FCSTD DOCUMENT  (FreeCAD 0.19R22756 (Git))
Label: housing
License: All rights reserved
LicenseURL: http://en.wikipedia.org/wiki/All_rights_reserved
objects: Part::Part2DObjectPython×38, Part::Extrusion×25, Part::Box×21, Part::Cut×11, Part::Cylinder×8, App::Part×8, Part::Compound×1, App::LinkGroup×1, Part::FeaturePython×1
note: 104 computed .brp shape members not serialized (recipe doc carries the construction recipe); baked Part::Feature solids carry a one-line shape summary decoded from their .brp

FEATURE [Part::Box] Box003  label="Cube003"
  AttacherType = Attacher::AttachEngine3D
  Height = 14
  Length = 125
  Placement = pos=(2,0,1) rot=(0,0,1;1.5708rad)
  Width = 1
FEATURE [Part::Box] Box006  label="Cube006"
  AttacherType = Attacher::AttachEngine3D
  Height = 1
  Length = 118
  Placement = pos=(1,1,1) rot=(0,0,1;0rad)
  Width = 123
FEATURE [Part::Cylinder] Cylinder
  Angle = 360
  AttacherType = Attacher::AttachEngine3D
  Height = 1.6
  Placement = pos=(0,0,5) rot=(0,0,1;0rad)
  Radius = 1
FEATURE [Part::Cylinder] Cylinder001
  Angle = 360
  AttacherType = Attacher::AttachEngine3D
  Height = 3
  Placement = pos=(0,0,2) rot=(0,0,1;0rad)
  Radius = 2
FEATURE [App::Part] Part001  label="Pod"
  Group = -> [Cylinder001,Cylinder]
  Origin = -> Origin001
  Placement = pos=(4.5,92,-1) rot=(0,0,1;0rad)
FEATURE [Part::Cylinder] Cylinder002
  Angle = 360
  AttacherType = Attacher::AttachEngine3D
  Height = 3
  Placement = pos=(0,0,2) rot=(0,0,1;0rad)
  Radius = 2
FEATURE [Part::Cylinder] Cylinder003
  Angle = 360
  AttacherType = Attacher::AttachEngine3D
  Height = 1.6
  Placement = pos=(0,0,5) rot=(0,0,1;0rad)
  Radius = 1
FEATURE [App::Part] Part002  label="Pod001"
  Group = -> [Cylinder002,Cylinder003]
  Origin = -> Origin002
  Placement = pos=(4.5,67,-1) rot=(0,0,1;0rad)
FEATURE [Part::Cylinder] Cylinder004
  Angle = 360
  AttacherType = Attacher::AttachEngine3D
  Height = 3
  Placement = pos=(0,0,2) rot=(0,0,1;0rad)
  Radius = 2
FEATURE [Part::Cylinder] Cylinder005
  Angle = 360
  AttacherType = Attacher::AttachEngine3D
  Height = 3
  Placement = pos=(0,0,2) rot=(0,0,1;0rad)
  Radius = 2
FEATURE [Part::Cylinder] Cylinder006
  Angle = 360
  AttacherType = Attacher::AttachEngine3D
  Height = 1.6
  Placement = pos=(0,0,5) rot=(0,0,1;0rad)
  Radius = 1
FEATURE [Part::Cylinder] Cylinder007
  Angle = 360
  AttacherType = Attacher::AttachEngine3D
  Height = 1.6
  Placement = pos=(0,0,5) rot=(0,0,1;0rad)
  Radius = 1
FEATURE [App::Part] Part003  label="Pod002"
  Group = -> [Cylinder004,Cylinder007]
  Origin = -> Origin003
  Placement = pos=(56.5,67,-1) rot=(0,0,1;0rad)
FEATURE [App::Part] Part004  label="Pod003"
  Group = -> [Cylinder005,Cylinder006]
  Origin = -> Origin004
  Placement = pos=(56.5,92,-1) rot=(0,0,1;0rad)
FEATURE [Part::Box] Box007  label="Cube007"
  AttacherType = Attacher::AttachEngine3D
  Height = 7
  Length = 2
  Placement = pos=(0,39,3.2) rot=(0,0,1;0rad)
  Width = 11
FEATURE [Part::Cut] Cut002
  Base = -> Box003
  Placement = pos=(118,0,-1) rot=(0,0,1;0rad)
  Tool = -> Box007
FEATURE [Part::Part2DObjectPython] ShapeString  # Draft 2D object (typed FeaturePython)
  FontFile = <userpath>/proj/esp8266_wordclock/hardware/lettering_plates/fonts/Taurus-Mono-Stencil-Bold.ttf
  Placement = pos=(151.6,102.2,0) rot=(0,0,1;0rad)
  Size = 3.5
  String = HETLISEBĲNA
  Tracking = 1
FEATURE [Part::Part2DObjectPython] ShapeString001  # Draft 2D object (typed FeaturePython)
  FontFile = <userpath>/proj/esp8266_wordclock/hardware/lettering_plates/fonts/Taurus-Mono-Stencil-Bold.ttf
  Placement = pos=(151.6,92.2,0) rot=(0,0,1;0rad)
  Size = 3.5
  String = NUSKWARTIEN
  Tracking = 1
FEATURE [Part::Part2DObjectPython] ShapeString002  # Draft 2D object (typed FeaturePython)
  FontFile = <userpath>/proj/esp8266_wordclock/hardware/lettering_plates/fonts/Taurus-Mono-Stencil-Bold.ttf
  Placement = pos=(151.6,82.2,0) rot=(0,0,1;0rad)
  Size = 3.5
  String = VIJFXRVOORN
  Tracking = 1
FEATURE [Part::Part2DObjectPython] ShapeString003  # Draft 2D object (typed FeaturePython)
  FontFile = <userpath>/proj/esp8266_wordclock/hardware/lettering_plates/fonts/Taurus-Mono-Stencil-Bold.ttf
  Placement = pos=(151.6,72.2,0) rot=(0,0,1;0rad)
  Size = 3.5
  String = OVERXZHALFD
  Tracking = 1
FEATURE [Part::Part2DObjectPython] ShapeString004  # Draft 2D object (typed FeaturePython)
  FontFile = <userpath>/proj/esp8266_wordclock/hardware/lettering_plates/fonts/Taurus-Mono-Stencil-Bold.ttf
  Placement = pos=(151.6,62.2,0) rot=(0,0,1;0rad)
  Size = 3.5
  String = ZESTWAALFSE
  Tracking = 1
FEATURE [Part::Part2DObjectPython] ShapeString005  # Draft 2D object (typed FeaturePython)
  FontFile = <userpath>/proj/esp8266_wordclock/hardware/lettering_plates/fonts/Taurus-Mono-Stencil-Bold.ttf
  Placement = pos=(151.6,52.2,0) rot=(0,0,1;0rad)
  Size = 3.5
  String = DRIEVIEREEN
  Tracking = 1
FEATURE [Part::Part2DObjectPython] ShapeString006  # Draft 2D object (typed FeaturePython)
  FontFile = <userpath>/proj/esp8266_wordclock/hardware/lettering_plates/fonts/Taurus-Mono-Stencil-Bold.ttf
  Placement = pos=(151.6,42.2,0) rot=(0,0,1;0rad)
  Size = 3.5
  String = TWEEEWACHTR
  Tracking = 1
FEATURE [Part::Part2DObjectPython] ShapeString007  # Draft 2D object (typed FeaturePython)
  FontFile = <userpath>/proj/esp8266_wordclock/hardware/lettering_plates/fonts/Taurus-Mono-Stencil-Bold.ttf
  Placement = pos=(151.6,32.2,0) rot=(0,0,1;0rad)
  Size = 3.5
  String = ZEVENEGENBM
  Tracking = 1
FEATURE [Part::Part2DObjectPython] ShapeString008  # Draft 2D object (typed FeaturePython)
  FontFile = <userpath>/proj/esp8266_wordclock/hardware/lettering_plates/fonts/Taurus-Mono-Stencil-Bold.ttf
  Placement = pos=(151.6,22.2,0) rot=(0,0,1;0rad)
  Size = 3.5
  String = TIENELFVIJF
  Tracking = 1
FEATURE [Part::Part2DObjectPython] ShapeString009  # Draft 2D object (typed FeaturePython)
  FontFile = <userpath>/proj/esp8266_wordclock/hardware/lettering_plates/fonts/Taurus-Mono-Stencil-Bold.ttf
  Placement = pos=(151.6,12.2,0) rot=(0,0,1;0rad)
  Size = 3.5
  String = CUURLBYPRMW
  Tracking = 1
FEATURE [Part::Part2DObjectPython] ShapeString010  # Draft 2D object (typed FeaturePython)
  FontFile = <userpath>/proj/esp8266_wordclock/hardware/lettering_plates/fonts/Taurus-Mono-Stencil-Bold.ttf
  Placement = pos=(151.6,2.2,0) rot=(0,0,1;0rad)
  Size = 3.5
  String = ALGEWEESTKP
  Tracking = 1
FEATURE [Part::Box] Box008  label="vent hole"
  AttacherType = Attacher::AttachEngine3D
  Height = 2
  Length = 20
  Placement = pos=(4,4,0) rot=(0,0,1;0rad)
  Width = 2
FEATURE [Part::Box] Box009  label="vent hole001"
  AttacherType = Attacher::AttachEngine3D
  Height = 2
  Length = 20
  Placement = pos=(96,4,0) rot=(0,0,1;0rad)
  Width = 2
FEATURE [Part::Box] Box010  label="vent hole002"
  AttacherType = Attacher::AttachEngine3D
  Height = 2
  Length = 20
  Placement = pos=(34,4,0) rot=(0,0,1;0rad)
  Width = 2
FEATURE [Part::Box] Box011  label="vent hole003"
  AttacherType = Attacher::AttachEngine3D
  Height = 2
  Length = 20
  Placement = pos=(66,4,0) rot=(0,0,1;0rad)
  Width = 2
FEATURE [Part::Box] Box012  label="vent hole004"
  AttacherType = Attacher::AttachEngine3D
  Height = 2
  Length = 20
  Placement = pos=(4,114,0) rot=(0,0,1;0rad)
  Width = 2
FEATURE [Part::Box] Box013  label="vent hole005"
  AttacherType = Attacher::AttachEngine3D
  Height = 2
  Length = 20
  Placement = pos=(96,114,0) rot=(0,0,1;0rad)
  Width = 2
FEATURE [Part::Box] Box014  label="vent hole006"
  AttacherType = Attacher::AttachEngine3D
  Height = 2
  Length = 20
  Placement = pos=(34,114,0) rot=(0,0,1;0rad)
  Width = 2
FEATURE [Part::Box] Box015  label="vent hole007"
  AttacherType = Attacher::AttachEngine3D
  Height = 2
  Length = 20
  Placement = pos=(66,114,0) rot=(0,0,1;0rad)
  Width = 2
FEATURE [App::Part] Part007  label="vent"
  Group = -> [Box009,Box010,Box011,Box014,Box013,Box012,Box015,Box008]
  Origin = -> Origin007
FEATURE [Part::Cut] Cut003
  Base = -> Box006
  Tool = -> Part007
FEATURE [Part::Box] Box018  label="Cube010"
  AttacherType = Attacher::AttachEngine3D
  Height = 5
  Length = 3.2
  Placement = pos=(115.5,114.5,9) rot=(0,0,1;0rad)
  Width = 2
FEATURE [Part::Box] Box019  label="Cube011"
  AttacherType = Attacher::AttachEngine3D
  Height = 5
  Length = 3.2
  Placement = pos=(115.5,6.5,9) rot=(0,0,1;0rad)
  Width = 2
FEATURE [Part::Box] Box020  label="Cube012"
  AttacherType = Attacher::AttachEngine3D
  Height = 5
  Length = 3.2
  Placement = pos=(1.3,6.5,9) rot=(0,0,1;0rad)
  Width = 2
FEATURE [Part::Box] Box021  label="Cube013"
  AttacherType = Attacher::AttachEngine3D
  Height = 5
  Length = 3.2
  Placement = pos=(1.3,114.5,9) rot=(0,0,1;0rad)
  Width = 2
FEATURE [Part::Part2DObjectPython] Rectangle  # Draft 2D object (typed FeaturePython)
  Area = 0
  ChamferSize = 0
  Columns = 1
  FilletRadius = 0
  Height = 125
  Length = 120
  MakeFace = false
  Placement = pos=(146,-5,0) rot=(0,0,1;0rad)
  Rows = 1
FEATURE [Part::Part2DObjectPython] Ellipse  # Draft 2D object (typed FeaturePython)
  Area = 0
  FirstAngle = 0
  LastAngle = 0
  MajorRadius = 3
  MakeFace = false
  MinorRadius = 2.5
  Placement = pos=(206,115,0) rot=(0,0,1;0rad)
FEATURE [App::Part] Part005  label="letterplate"
  Group = -> [ShapeString009,ShapeString008,ShapeString004,ShapeString003,ShapeString002,ShapeString001,ShapeString007,ShapeString005,ShapeString006,ShapeString010,ShapeString,Rectangle,Ellipse]
  Origin = -> Origin005
  Placement = pos=(0,150,0) rot=(0,0,1;0rad)
FEATURE [Part::Part2DObjectPython] ShapeString024  # Draft 2D object (typed FeaturePython)
  FontFile = <userpath>/proj/esp8266_wordclock/hardware/lettering_plates/fonts/Taurus-Mono-Stencil-Bold.ttf
  Placement = pos=(151.6,82.2,0) rot=(0,0,1;0rad)
  Size = 3.5
  String = VIJFXRVOORN
  Tracking = 1
FEATURE [Part::Extrusion] Extrude017
  Base = -> ShapeString024
  Dir = (0,0,1)
  DirMode = 2
  FaceMakerClass = Part::FaceMakerBullseye
  LengthFwd = 1
  LengthRev = 0
  Solid = false
  Symmetric = false
FEATURE [Part::Part2DObjectPython] ShapeString027  # Draft 2D object (typed FeaturePython)
  FontFile = <userpath>/proj/esp8266_wordclock/hardware/lettering_plates/fonts/Taurus-Mono-Stencil-Bold.ttf
  Placement = pos=(151.6,52.2,0) rot=(0,0,1;0rad)
  Size = 3.5
  String = DRIEVIEREEN
  Tracking = 1
FEATURE [Part::Extrusion] Extrude020
  Base = -> ShapeString027
  Dir = (0,0,1)
  DirMode = 2
  FaceMakerClass = Part::FaceMakerBullseye
  LengthFwd = 1
  LengthRev = 0
  Solid = false
  Symmetric = false
FEATURE [Part::Part2DObjectPython] ShapeString023  # Draft 2D object (typed FeaturePython)
  FontFile = <userpath>/proj/esp8266_wordclock/hardware/lettering_plates/fonts/Taurus-Mono-Stencil-Bold.ttf
  Placement = pos=(151.6,92.2,0) rot=(0,0,1;0rad)
  Size = 3.5
  String = NUSKWARTIEN
  Tracking = 1
FEATURE [Part::Part2DObjectPython] ShapeString032  # Draft 2D object (typed FeaturePython)
  FontFile = <userpath>/proj/esp8266_wordclock/hardware/lettering_plates/fonts/Taurus-Mono-Stencil-Bold.ttf
  Placement = pos=(151.6,2.2,0) rot=(0,0,1;0rad)
  Size = 3.5
  String = ALGEWEESTKP
  Tracking = 1
FEATURE [Part::Part2DObjectPython] ShapeString025  # Draft 2D object (typed FeaturePython)
  FontFile = <userpath>/proj/esp8266_wordclock/hardware/lettering_plates/fonts/Taurus-Mono-Stencil-Bold.ttf
  Placement = pos=(151.6,72.2,0) rot=(0,0,1;0rad)
  Size = 3.5
  String = OVERXZHALFD
  Tracking = 1
FEATURE [Part::Extrusion] Extrude018
  Base = -> ShapeString025
  Dir = (0,0,1)
  DirMode = 2
  FaceMakerClass = Part::FaceMakerBullseye
  LengthFwd = 1
  LengthRev = 0
  Solid = false
  Symmetric = false
FEATURE [Part::Part2DObjectPython] ShapeString029  # Draft 2D object (typed FeaturePython)
  FontFile = <userpath>/proj/esp8266_wordclock/hardware/lettering_plates/fonts/Taurus-Mono-Stencil-Bold.ttf
  Placement = pos=(151.6,32.2,0) rot=(0,0,1;0rad)
  Size = 3.5
  String = ZEVENEGENBM
  Tracking = 1
FEATURE [Part::Extrusion] Extrude022
  Base = -> ShapeString029
  Dir = (0,0,1)
  DirMode = 2
  FaceMakerClass = Part::FaceMakerBullseye
  LengthFwd = 1
  LengthRev = 0
  Solid = false
  Symmetric = false
FEATURE [Part::Part2DObjectPython] ShapeString026  # Draft 2D object (typed FeaturePython)
  FontFile = <userpath>/proj/esp8266_wordclock/hardware/lettering_plates/fonts/Taurus-Mono-Stencil-Bold.ttf
  Placement = pos=(151.6,62.2,0) rot=(0,0,1;0rad)
  Size = 3.5
  String = ZESTWAALFSE
  Tracking = 1
FEATURE [Part::Extrusion] Extrude025
  Base = -> ShapeString032
  Dir = (0,0,1)
  DirMode = 2
  FaceMakerClass = Part::FaceMakerBullseye
  LengthFwd = 1
  LengthRev = 0
  Solid = false
  Symmetric = false
FEATURE [Part::Part2DObjectPython] ShapeString031  # Draft 2D object (typed FeaturePython)
  FontFile = <userpath>/proj/esp8266_wordclock/hardware/lettering_plates/fonts/Taurus-Mono-Stencil-Bold.ttf
  Placement = pos=(151.6,12.2,0) rot=(0,0,1;0rad)
  Size = 3.5
  String = CUURLBYPRMW
  Tracking = 1
FEATURE [Part::Extrusion] Extrude024
  Base = -> ShapeString031
  Dir = (0,0,1)
  DirMode = 2
  FaceMakerClass = Part::FaceMakerBullseye
  LengthFwd = 1
  LengthRev = 0
  Solid = false
  Symmetric = false
FEATURE [Part::Part2DObjectPython] ShapeString030  # Draft 2D object (typed FeaturePython)
  FontFile = <userpath>/proj/esp8266_wordclock/hardware/lettering_plates/fonts/Taurus-Mono-Stencil-Bold.ttf
  Placement = pos=(151.6,22.2,0) rot=(0,0,1;0rad)
  Size = 3.5
  String = TIENELFVIJF
  Tracking = 1
FEATURE [Part::Extrusion] Extrude023
  Base = -> ShapeString030
  Dir = (0,0,1)
  DirMode = 2
  FaceMakerClass = Part::FaceMakerBullseye
  LengthFwd = 1
  LengthRev = 0
  Solid = false
  Symmetric = false
FEATURE [Part::Part2DObjectPython] ShapeString028  # Draft 2D object (typed FeaturePython)
  FontFile = <userpath>/proj/esp8266_wordclock/hardware/lettering_plates/fonts/Taurus-Mono-Stencil-Bold.ttf
  Placement = pos=(151.6,42.2,0) rot=(0,0,1;0rad)
  Size = 3.5
  String = TWEEEWACHTR
  Tracking = 1
FEATURE [Part::Extrusion] Extrude021
  Base = -> ShapeString028
  Dir = (0,0,1)
  DirMode = 2
  FaceMakerClass = Part::FaceMakerBullseye
  LengthFwd = 1
  LengthRev = 0
  Solid = false
  Symmetric = false
FEATURE [Part::Part2DObjectPython] Rectangle002  # Draft 2D object (typed FeaturePython)
  Area = 0
  ChamferSize = 0
  Columns = 1
  FilletRadius = 0
  Height = 125
  Length = 120
  MakeFace = false
  Placement = pos=(146,-5,0) rot=(0,0,1;0rad)
  Rows = 1
FEATURE [Part::Extrusion] Extrude013
  Base = -> Rectangle002
  Dir = (0,0,1)
  DirMode = 2
  FaceMakerClass = Part::FaceMakerBullseye
  LengthFwd = 1
  LengthRev = 0
  Solid = true
  Symmetric = false
FEATURE [Part::Part2DObjectPython] ShapeString022  # Draft 2D object (typed FeaturePython)
  FontFile = <userpath>/proj/esp8266_wordclock/hardware/lettering_plates/fonts/Taurus-Mono-Stencil-Bold.ttf
  Placement = pos=(151.6,102.2,0) rot=(0,0,1;0rad)
  Size = 3.5
  String = HETLISEBĲNA
  Tracking = 1
FEATURE [Part::Extrusion] Extrude015
  Base = -> ShapeString022
  Dir = (0,0,1)
  DirMode = 2
  FaceMakerClass = Part::FaceMakerBullseye
  LengthFwd = 1
  LengthRev = 0
  Solid = false
  Symmetric = false
FEATURE [Part::Extrusion] Extrude016
  Base = -> ShapeString023
  Dir = (0,0,1)
  DirMode = 2
  FaceMakerClass = Part::FaceMakerBullseye
  LengthFwd = 1
  LengthRev = 0
  Solid = false
  Symmetric = false
FEATURE [Part::Extrusion] Extrude019
  Base = -> ShapeString026
  Dir = (0,0,1)
  DirMode = 2
  FaceMakerClass = Part::FaceMakerBullseye
  LengthFwd = 1
  LengthRev = 0
  Solid = false
  Symmetric = false
FEATURE [Part::Part2DObjectPython] Ellipse001  # Draft 2D object (typed FeaturePython)
  Area = 0
  FirstAngle = 0
  LastAngle = 0
  MajorRadius = 3
  MakeFace = false
  MinorRadius = 2.5
  Placement = pos=(206,115,0) rot=(0,0,1;0rad)
FEATURE [Part::Extrusion] Extrude
  Base = -> Ellipse001
  Dir = (0,0,1)
  DirMode = 2
  FaceMakerClass = Part::FaceMakerBullseye
  LengthFwd = 1
  LengthRev = 0
  Solid = true
  Symmetric = false
FEATURE [Part::Compound] Compound
  Links = -> [Extrude015,Extrude016,Extrude017,Extrude018,Extrude019,Extrude020,Extrude021,Extrude022,Extrude023,Extrude024,Extrude025,Extrude]
FEATURE [Part::Cut] Cut016  label="Letterplate"
  Base = -> Extrude013
  Placement = pos=(-146,5,14) rot=(0,0,1;0rad)
  Tool = -> Compound
FEATURE [Part::Part2DObjectPython] Rectangle003  # Draft 2D object (typed FeaturePython)
  Area = 0
  ChamferSize = 0
  Columns = 1
  FilletRadius = 0
  Height = 125
  Length = 1
  MakeFace = false
  Placement = pos=(146,-5,0) rot=(0,0,1;0rad)
  Rows = 1
FEATURE [Part::Extrusion] Extrude026
  Base = -> Rectangle003
  Dir = (0,0,1)
  DirMode = 2
  FaceMakerClass = Part::FaceMakerBullseye
  LengthFwd = -14
  LengthRev = 0
  Placement = pos=(-146,5,14) rot=(0,0,1;0rad)
  Solid = true
  Symmetric = false
FEATURE [Part::Part2DObjectPython] Rectangle005  # Draft 2D object (typed FeaturePython)
  Area = 0
  ChamferSize = 0
  Columns = 1
  FilletRadius = 0
  Height = 1
  Length = 118
  MakeFace = false
  Placement = pos=(147,-5,0) rot=(0,0,1;0rad)
  Rows = 1
FEATURE [Part::Part2DObjectPython] Rectangle006  # Draft 2D object (typed FeaturePython)
  Area = 0
  ChamferSize = 0
  Columns = 1
  FilletRadius = 0
  Height = 1
  Length = 118
  MakeFace = false
  Placement = pos=(147,119,0) rot=(0,0,1;0rad)
  Rows = 1
FEATURE [Part::Extrusion] Extrude028
  Base = -> Rectangle005
  Dir = (0,0,1)
  DirMode = 2
  FaceMakerClass = Part::FaceMakerBullseye
  LengthFwd = -14
  LengthRev = 0
  Placement = pos=(-146,5,14) rot=(0,0,1;0rad)
  Solid = true
  Symmetric = false
FEATURE [Part::Extrusion] Extrude029
  Base = -> Rectangle006
  Dir = (0,0,1)
  DirMode = 2
  FaceMakerClass = Part::FaceMakerBullseye
  LengthFwd = -14
  LengthRev = 0
  Placement = pos=(-146,5,14) rot=(0,0,1;0rad)
  Solid = true
  Symmetric = false
FEATURE [Part::Part2DObjectPython] Rectangle008  # Draft 2D object (typed FeaturePython)
  Area = 0
  ChamferSize = 0
  Columns = 1
  FilletRadius = 0
  Height = 1
  Length = 118
  MakeFace = false
  Placement = pos=(147,1,0) rot=(0,0,1;0rad)
  Rows = 1
FEATURE [Part::Extrusion] Extrude031
  Base = -> Rectangle008
  Dir = (0,0,1)
  DirMode = 2
  FaceMakerClass = Part::FaceMakerBullseye
  LengthFwd = -13
  LengthRev = 0
  Placement = pos=(-146,4.5,14) rot=(0,0,1;0rad)
  Solid = true
  Symmetric = false
FEATURE [Part::Box] Box023  label="Cube015"
  AttacherType = Attacher::AttachEngine3D
  Height = 13
  Length = 5
  Placement = pos=(147,-4,-13) rot=(0,0,1;0rad)
  Width = 5
FEATURE [Part::Box] Box024  label="Cube016"
  AttacherType = Attacher::AttachEngine3D
  Height = 13
  Length = 5
  Placement = pos=(260,-4,-13) rot=(0,0,1;0rad)
  Width = 5
FEATURE [Part::Part2DObjectPython] Circle  # Draft 2D object (typed FeaturePython)
  Area = 0
  FirstAngle = 0
  LastAngle = 0
  MakeFace = false
  Placement = pos=(150,116,-13) rot=(0,0,1;0rad)
  Radius = 0.5
FEATURE [Part::Part2DObjectPython] Circle001  # Draft 2D object (typed FeaturePython)
  Area = 0
  FirstAngle = 0
  LastAngle = 0
  MakeFace = false
  Placement = pos=(150,116,-13) rot=(0,0,1;0rad)
  Radius = 0.5
FEATURE [Part::Extrusion] Extrude033
  Base = -> Circle001
  Dir = (0,0,1)
  DirMode = 2
  FaceMakerClass = Part::FaceMakerBullseye
  LengthFwd = 7
  LengthRev = 0
  Placement = pos=(0,-117,0) rot=(0,0,1;0rad)
  Solid = true
  Symmetric = false
FEATURE [Part::Part2DObjectPython] Circle002  # Draft 2D object (typed FeaturePython)
  Area = 0
  FirstAngle = 0
  LastAngle = 0
  MakeFace = false
  Placement = pos=(150,116,-13) rot=(0,0,1;0rad)
  Radius = 0.5
FEATURE [Part::Extrusion] Extrude035
  Base = -> Circle002
  Dir = (0,0,1)
  DirMode = 2
  FaceMakerClass = Part::FaceMakerBullseye
  LengthFwd = 7
  LengthRev = 0
  Placement = pos=(112,-117,0) rot=(0,0,1;0rad)
  Solid = true
  Symmetric = false
FEATURE [Part::Part2DObjectPython] Circle003  # Draft 2D object (typed FeaturePython)
  Area = 0
  FirstAngle = 0
  LastAngle = 0
  MakeFace = false
  Placement = pos=(150,116,-13) rot=(0,0,1;0rad)
  Radius = 0.5
FEATURE [Part::Box] Box022  label="Cube014"
  AttacherType = Attacher::AttachEngine3D
  Height = 13
  Length = 5
  Placement = pos=(260,112.3,-13) rot=(0,0,1;0rad)
  Width = 7.2
FEATURE [Part::Extrusion] Extrude034
  Base = -> Circle003
  Dir = (0,0,1)
  DirMode = 2
  FaceMakerClass = Part::FaceMakerBullseye
  LengthFwd = 7
  LengthRev = 0
  Placement = pos=(112,0.5,0) rot=(0,0,1;0rad)
  Solid = true
  Symmetric = false
FEATURE [Part::Box] Box016  label="Cube008"
  AttacherType = Attacher::AttachEngine3D
  Height = 13
  Length = 5
  Placement = pos=(147,111.7,-13) rot=(0,0,1;0rad)
  Width = 7.2
FEATURE [Part::Extrusion] Extrude032
  Base = -> Circle
  Dir = (0,0,1)
  DirMode = 2
  FaceMakerClass = Part::FaceMakerBullseye
  LengthFwd = 7
  LengthRev = 0
  Placement = pos=(0,-0.1,0) rot=(0,0,1;0rad)
  Solid = true
  Symmetric = false
FEATURE [Part::Cut] Cut017
  Base = -> Box016
  Placement = pos=(-146,5.1,14) rot=(0,0,1;0rad)
  Tool = -> Extrude032
FEATURE [Part::Cut] Cut018
  Base = -> Box023
  Placement = pos=(-146,5,14) rot=(0,0,1;0rad)
  Tool = -> Extrude033
FEATURE [Part::Cut] Cut019
  Base = -> Box022
  Placement = pos=(-146,4.5,14) rot=(0,0,1;0rad)
  Tool = -> Extrude034
FEATURE [Part::Cut] Cut020
  Base = -> Box024
  Placement = pos=(-146,5,14) rot=(0,0,1;0rad)
  Tool = -> Extrude035
FEATURE [App::LinkGroup] LinkGroup  label="letterbox"
  ElementList = -> [Cut017,Extrude031,Extrude026,Cut016,Cut019,Extrude029,Cut020,Extrude028,Cut018,Cut002]
  LinkMode = 0
  Placement = pos=(0,0,80) rot=(0,0,1;0rad)
FEATURE [Part::Part2DObjectPython] Rectangle009  # Draft 2D object (typed FeaturePython)
  Area = 0
  ChamferSize = 0
  Columns = 1
  FilletRadius = 0
  Height = 65
  Length = 45
  MakeFace = false
  Rows = 1
FEATURE [Part::Extrusion] Extrude036
  Base = -> Rectangle009
  Dir = (0,0,1)
  DirMode = 2
  FaceMakerClass = Part::FaceMakerBullseye
  LengthFwd = 1
  LengthRev = 0
  Placement = pos=(60,37,1) rot=(0,0,1;0rad)
  Solid = true
  Symmetric = false
FEATURE [Part::Cut] Cut021
  Base = -> Cut003
  Placement = pos=(0,0,-1) rot=(0,0,1;0rad)
  Tool = -> Extrude036
FEATURE [App::Part] Part006  label="back"
  Group = -> [Part002,Part003,Box006,Part007,Cut003,Rectangle009,Extrude036,Cut021,Part001,Part004]
  Origin = -> Origin006
FEATURE [Part::Part2DObjectPython] Rectangle010  # Draft 2D object (typed FeaturePython)
  Area = 0
  ChamferSize = 0
  Columns = 1
  FilletRadius = 0
  Height = 65
  Length = 45
  MakeFace = false
  Placement = pos=(60,37,2) rot=(0,0,1;0rad)
  Rows = 1
FEATURE [Part::Part2DObjectPython] Rectangle011  # Draft 2D object (typed FeaturePython)
  Area = 0
  ChamferSize = 0
  Columns = 1
  FilletRadius = 0
  Height = 67
  Length = 47
  MakeFace = false
  Placement = pos=(59,36,2) rot=(0,0,1;0rad)
  Rows = 1
FEATURE [Part::Extrusion] Extrude037
  Base = -> Rectangle011
  Dir = (0,0,1)
  DirMode = 2
  FaceMakerClass = Part::FaceMakerBullseye
  LengthFwd = 6
  LengthRev = 0
  Solid = true
  Symmetric = false
FEATURE [Part::Extrusion] Extrude038
  Base = -> Rectangle010
  Dir = (0,0,1)
  DirMode = 2
  FaceMakerClass = Part::FaceMakerBullseye
  LengthFwd = 5
  LengthRev = 0
  Solid = true
  Symmetric = false
FEATURE [Part::Cut] Cut022
  Base = -> Extrude037
  Placement = pos=(0,0,-1) rot=(0,0,1;0rad)
  Tool = -> Extrude038
FEATURE [Part::Part2DObjectPython] Rectangle012  # Draft 2D object (typed FeaturePython)
  Area = 0
  ChamferSize = 0
  Columns = 1
  FilletRadius = 0
  Height = 6
  Length = 1
  MakeFace = false
  Placement = pos=(58,76.5,2) rot=(0,0,1;0rad)
  Rows = 1
FEATURE [Part::Extrusion] Extrude039
  Base = -> Rectangle012
  Dir = (0,0,1)
  DirMode = 2
  FaceMakerClass = Part::FaceMakerBullseye
  LengthFwd = 3
  LengthRev = 0
  Placement = pos=(1,0,0) rot=(0,0,1;0rad)
  Solid = true
  Symmetric = false
FEATURE [Part::Cut] Cut023  label="backsink"
  Base = -> Cut022
  Tool = -> Extrude039
FEATURE [Part::Box] Box025  label="Cube017"
  AttacherType = Attacher::AttachEngine3D
  Height = 5
  Length = 9
  Placement = pos=(1,0,0) rot=(0,0,1;0rad)
  Width = 9
FEATURE [Part::Box] Box026  label="Cube018"
  AttacherType = Attacher::AttachEngine3D
  Height = 5
  Length = 111
  Width = 110
FEATURE [Part::FeaturePython] Array001  # Draft array (typed FeaturePython)
  Angle = 360
  ArrayType = 0
  Axis = (0,0,1)
  Base = -> Box025
  Center = (0,0,0)
  Count = 121
  ExpandArray = false
  Fuse = false
  IntervalAxis = (0,0,0)
  IntervalX = (10,0,0)
  IntervalY = (0,10,0)
  IntervalZ = (0,0,100)
  NumberCircles = 3
  NumberPolar = 5
  NumberX = 11
  NumberY = 11
  NumberZ = 1
  PlacementList = 121 placements: [(1,0,0),(1,10,0),(1,20,0),(1,30,0),(1,40,0),(1,50,0),(1,60,0),(1,70,0),(1,80,0),(1,90,0),(1,100,0),(11,0,0),(11,10,0),(11,20,0),(11,30,0),(11,40,0),(11,50,0),(11,60,0),(11,70,0),(11,80,0),(11,90,0),(11,100,0),(21,0,0),(21,10,0),(21,20,0),(21,30,0),(21,40,0),(21,50,0),(21,60,0),(21,70,0),(21,80,0),(21,90,0),(21,100,0),(31,0,0),(31,10,0),(31,20,0),(31,30,0),(31,40,0),(31,50,0),(31,60,0),(31,70,0),+80 more]
  RadialDistance = 50
  ScaleList = (121) [(1,1,1),(1,1,1),(1,1,1),(1,1,1),(1,1,1),(1,1,1),(1,1,1),(1,1,1),(1,1,1),(1,1,1),(1,1,1),(1,1,1),(1,1,1),(1,1,1),(1,1,1),(1,1,1),(1,1,1),(1,1,1),+103 more]
  Symmetry = 1
  TangentialDistance = 25
FEATURE [Part::Cut] Cut
  Base = -> Box026
  Placement = pos=(4.5,6.5,9) rot=(0,0,1;0rad)
  Tool = -> Array001
FEATURE [App::Part] Part  label="Raster"
  Group = -> [Box018,Box021,Box019,Box020,Box026,Array001,Box025,Cut]
  Origin = -> Origin
  Placement = pos=(0,0,50) rot=(0,0,1;0rad)
